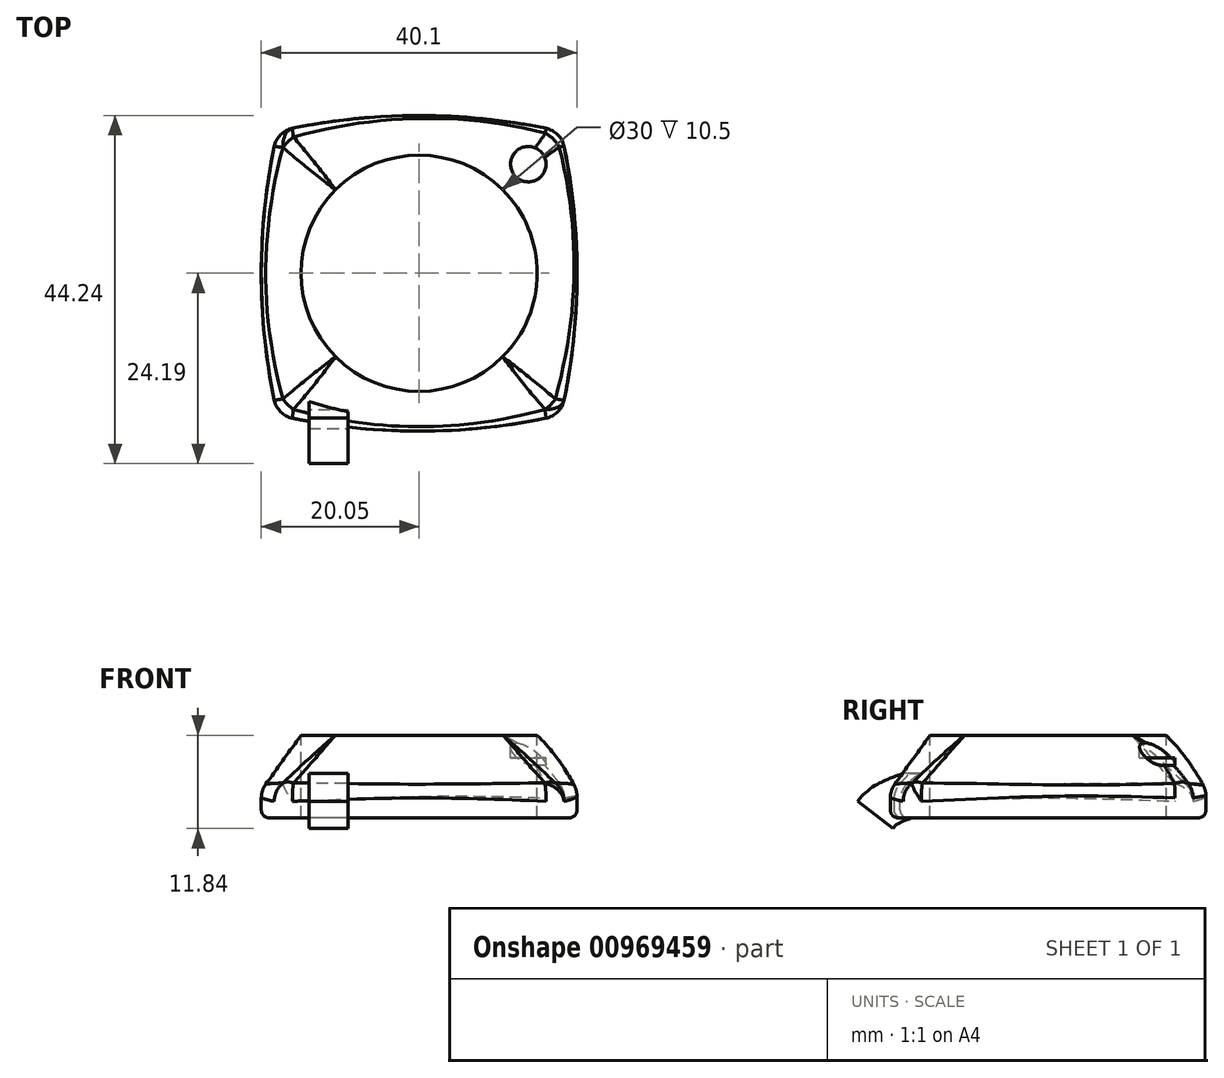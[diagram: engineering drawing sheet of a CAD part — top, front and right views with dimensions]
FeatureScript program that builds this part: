
annotation { "Feature Type Name" : "Feature", "Feature Type Description" : "" }
export const myFeature = defineFeature(function(context is Context, id is Id, definition is map)
    precondition{}
    {
        {
            assignVariable(context, id + "F0", {"name" : "base", "anyValue" : .333});
        }
        {
            assignVariable(context, id + "F1", {"name" : "Height", "anyValue" : 10.5});
        }
        {
            assignVariable(context, id + "F2", {"name" : "depth", "anyValue" : 2.9});
        }
        {
            var Q0;
            Q0=qCreatedBy(makeId("Top.planeOp"),FACE);
            var sketch = newSketch(context, id + "F3", { "sketchPlane" : qUnion([Q0])});
            skLineSegment(sketch, "E0.bottom", {"start": v(18, 18) * mm, "end": v(-18, 18) * mm});
            skLineSegment(sketch, "E0.top", {"start": v(18, -18) * mm, "end": v(-18, -18) * mm});
            skLineSegment(sketch, "E0.left", {"start": v(18, 18) * mm, "end": v(18, -18) * mm});
            skLineSegment(sketch, "E0.right", {"start": v(-18, 18) * mm, "end": v(-18, -18) * mm});
            skPoint(sketch, "E0.middle", {"position": v(0, 0) * mm});
            skArc(sketch, "E1", {"start": v(-18, 18) * mm, "mid": v(-20.05, 0) * mm, "end": v(-18, -18) * mm});
            skArc(sketch, "E2", {"start": v(18, 18) * mm, "mid": v(0, 20.05) * mm, "end": v(-18, 18) * mm});
            skArc(sketch, "E3.MirrorCS", {"start": v(18, -18) * mm, "mid": v(0, -20.05) * mm, "end": v(-18, -18) * mm});
            skArc(sketch, "E4.MirrorCS", {"start": v(18, 18) * mm, "mid": v(20.05, 0) * mm, "end": v(18, -18) * mm});
            skLineSegment(sketch, "E5", {"start": v(-18, 18) * mm, "end": v(18, -18) * mm, "construction": true});
            skLineSegment(sketch, "E6", {"start": v(18, 18) * mm, "end": v(-18, -18) * mm, "construction": true});
            skSolve(sketch);
        }
        {
            var Q0;
            Q0=qCreatedBy(makeId("Top.planeOp"),FACE);
            cPlane(context, id + "F4", {"entities" : qUnion([Q0]), "cplaneType" : CPlaneType.OFFSET, "offset" : ((1 - getVariable(context, 'base')) * getVariable(context, 'Height')) * mm, "width" : 150 * mm, "height" : 150 * mm});
        }
        {
            var Q0;
            Q0 = qSketchRegion(id + "F3", true);
            extrude(context, id + "F5", {"entities" : qUnion([Q0]), "oppositeDirection" : true, "depth" : (getVariable(context, 'base') * getVariable(context, 'Height')) * mm, "offsetDistance" : 25 * mm});
        }
        {
            var Q0;
            Q0=qCreatedBy(id+"F4.planeOp",FACE);
            var sketch = newSketch(context, id + "F6", { "sketchPlane" : qUnion([Q0])});
            skCircle(sketch, "E7", {"center": v(0, 0) * mm, "radius": 15 * mm});
            skPoint(sketch, "E8", {"position": v(15, 0) * mm});
            skPoint(sketch, "E9.1.0", {"position": v(10.6, 10.6) * mm});
            skPoint(sketch, "E9.2.0", {"position": v(0, 15) * mm});
            skPoint(sketch, "E9.3.0", {"position": v(-10.6, 10.6) * mm});
            skPoint(sketch, "E9.4.0", {"position": v(-15, 0) * mm});
            skPoint(sketch, "E9.5.0", {"position": v(-10.6, -10.6) * mm});
            skPoint(sketch, "E9.6.0", {"position": v(0, -15) * mm});
            skPoint(sketch, "E9.7.0", {"position": v(10.6, -10.6) * mm});
            skSolve(sketch);
        }
        {
            var Q0;
            Q0=makeQuery(id+"F5.opExtrude","SWEPT_EDGE",EDGE,{"disambiguationData":[OSD([sQuery(id+"F3.wireOp",EDGE,"E0.bottom"),sQuery(id+"F3.wireOp",EDGE,"E0.left"),sQuery(id+"F3.wireOp",EDGE,"E2"),sQuery(id+"F3.wireOp",EDGE,"E4.MirrorCS")])]});
            var Q1;
            Q1=sQuery(id+"F3.wireOp",VERTEX,"E0.middle");
            cPlane(context, id + "F7", {"entities" : qUnion([Q0, Q1]), "cplaneType" : CPlaneType.LINE_ANGLE, "offset" : 25 * mm, "angle" : 0 * degree, "oppositeDirection" : true, "width" : 150 * mm, "height" : 150 * mm});
        }
        {
            var Q0;
            Q0=qCreatedBy(id+"F7.planeOp",FACE);
            var sketch = newSketch(context, id + "F8", { "sketchPlane" : qUnion([Q0])});
            skArc(sketch, "E10", {"start": v(25.46, 0) * mm, "mid": v(20.68, 4.17) * mm, "end": v(15, 7) * mm});
            skLineSegment(sketch, "E11", {"start": v(0, 7.12) * mm, "end": v(0, 17.1) * mm});
            skSolve(sketch);
        }
        {
            var Q0;
            Q0=makeQuery(id+"F6.imprint","IMPRINT",FACE,{"disambiguationData":[TD([[makeQuery(id+"F6.imprint","IMPRINT",EDGE,{"derivedFrom":sQuery(id+"F6.wireOp",EDGE,"E7")}),1.0]])]});
            var Q1;
            Q1=makeQuery(id+"F5.opExtrude","CAP_FACE",FACE,{"disambiguationData":[OSD([sQuery(id+"F3.wireOp",EDGE,"E1"),sQuery(id+"F3.wireOp",EDGE,"E2"),sQuery(id+"F3.wireOp",EDGE,"E3.MirrorCS"),sQuery(id+"F3.wireOp",EDGE,"E4.MirrorCS")])],"isStart":true});
            var Q2;
            Q2=sQuery(id+"FI9qdWhZOXyrW1U_1.1.F8.wireOp",EDGE,"E10");
            var Q3;
            Q3=sQuery(id+"FI9qdWhZOXyrW1U_1.2.F8.wireOp",EDGE,"E10");
            var Q4;
            Q4=sQuery(id+"FI9qdWhZOXyrW1U_1.3.F8.wireOp",EDGE,"E10");
            var Q5;
            Q5=sQuery(id+"F8.wireOp",EDGE,"E10");
            loft(context, id + "F9", {"operationType" : NewBodyOperationType.ADD, "addGuides" : true, "sheetProfilesArray" : [{ "sheetProfileEntities" : qUnion([Q0]) }, { "sheetProfileEntities" : qUnion([Q1]) }], "guidesArray" : [{ "guideEntities" : qUnion([Q2]), "guideDerivativeType" : LoftGuideDerivativeType.DEFAULT, "guideDerivativeMagnitude" : 1 }, { "guideEntities" : qUnion([Q3]), "guideDerivativeType" : LoftGuideDerivativeType.DEFAULT, "guideDerivativeMagnitude" : 1 }, { "guideEntities" : qUnion([Q4]), "guideDerivativeType" : LoftGuideDerivativeType.DEFAULT, "guideDerivativeMagnitude" : 1 }, { "guideEntities" : qUnion([Q5]), "guideDerivativeType" : LoftGuideDerivativeType.DEFAULT, "guideDerivativeMagnitude" : 1 }]});
        }
        {
            var Q0;
            {var subQ0=sQuery(id+"F3.wireOp",EDGE,"E3.MirrorCS");Q0=makeQuery(id+"F9.boolean.opBoolean","MERGE",EDGE,{"derivedFrom":[makeQuery(id+"F5.opExtrude","CAP_EDGE",EDGE,{"disambiguationData":[OSD([subQ0])],"isStart":true}),makeQuery(id+"F9.opLoft","MID_CAP_EDGE",EDGE,{"disambiguationData":[OSD([sQuery(id+"F3.wireOp",EDGE,"E0.top"),sQuery(id+"F3.wireOp",EDGE,"E0.left"),sQuery(id+"F3.wireOp",EDGE,"E0.right"),sQuery(id+"F3.wireOp",EDGE,"E1"),subQ0,sQuery(id+"F3.wireOp",EDGE,"E4.MirrorCS")])],"capPos":1.0})]});}
            var Q1;
            {var subQ0=sQuery(id+"F3.wireOp",EDGE,"E4.MirrorCS");Q1=makeQuery(id+"F9.boolean.opBoolean","MERGE",EDGE,{"derivedFrom":[makeQuery(id+"F5.opExtrude","CAP_EDGE",EDGE,{"disambiguationData":[OSD([subQ0])],"isStart":true}),makeQuery(id+"F9.opLoft","MID_CAP_EDGE",EDGE,{"disambiguationData":[OSD([sQuery(id+"F3.wireOp",EDGE,"E0.bottom"),sQuery(id+"F3.wireOp",EDGE,"E0.top"),sQuery(id+"F3.wireOp",EDGE,"E0.left"),sQuery(id+"F3.wireOp",EDGE,"E2"),sQuery(id+"F3.wireOp",EDGE,"E3.MirrorCS"),subQ0])],"capPos":1.0})]});}
            var Q2;
            {var subQ0=sQuery(id+"F3.wireOp",EDGE,"E2");Q2=makeQuery(id+"F9.boolean.opBoolean","MERGE",EDGE,{"derivedFrom":[makeQuery(id+"F5.opExtrude","CAP_EDGE",EDGE,{"disambiguationData":[OSD([subQ0])],"isStart":true}),makeQuery(id+"F9.opLoft","MID_CAP_EDGE",EDGE,{"disambiguationData":[OSD([sQuery(id+"F3.wireOp",EDGE,"E0.bottom"),sQuery(id+"F3.wireOp",EDGE,"E0.left"),sQuery(id+"F3.wireOp",EDGE,"E0.right"),sQuery(id+"F3.wireOp",EDGE,"E1"),subQ0,sQuery(id+"F3.wireOp",EDGE,"E4.MirrorCS")])],"capPos":1.0})]});}
            var Q3;
            {var subQ0=sQuery(id+"F3.wireOp",EDGE,"E1");Q3=makeQuery(id+"F9.boolean.opBoolean","MERGE",EDGE,{"derivedFrom":[makeQuery(id+"F5.opExtrude","CAP_EDGE",EDGE,{"disambiguationData":[OSD([subQ0])],"isStart":true}),makeQuery(id+"F9.opLoft","MID_CAP_EDGE",EDGE,{"disambiguationData":[OSD([sQuery(id+"F3.wireOp",EDGE,"E0.bottom"),sQuery(id+"F3.wireOp",EDGE,"E0.top"),sQuery(id+"F3.wireOp",EDGE,"E0.right"),subQ0,sQuery(id+"F3.wireOp",EDGE,"E2"),sQuery(id+"F3.wireOp",EDGE,"E3.MirrorCS")])],"capPos":1.0})]});}
            fillet(context, id + "F10", {"entities" : qUnion([Q0, Q1, Q2, Q3]), "radius" : 3 * mm, "tangentPropagation" : true, "allowEdgeOverflow" : false});
        }
        {
            var Q0;
            Q0=makeQuery(id+"F6.imprint","IMPRINT",FACE,{"disambiguationData":[TD([[makeQuery(id+"F6.imprint","IMPRINT",EDGE,{"derivedFrom":sQuery(id+"F6.wireOp",EDGE,"E7")}),1.0]])]});
            var sketch = newSketch(context, id + "F11", { "sketchPlane" : qUnion([Q0])});
            skCircle(sketch, "E12", {"center": v(13.86, 13.86) * mm, "radius": 2.25 * mm});
            skLineSegment(sketch, "E13", {"start": v(10.6, 10.6) * mm, "end": v(13.86, 13.86) * mm, "construction": true});
            skPoint(sketch, "E14", {"position": v(10.6, 10.6) * mm});
            skSolve(sketch);
        }
        {
            var Q0;
            Q0=makeQuery(id+"F9.opLoft","SWEPT_EDGE",EDGE,{"disambiguationData":[OSD([sQuery(id+"F3.wireOp",EDGE,"E0.bottom"),sQuery(id+"F3.wireOp",EDGE,"E0.top"),sQuery(id+"F3.wireOp",EDGE,"E0.right"),sQuery(id+"F3.wireOp",EDGE,"E1"),sQuery(id+"F3.wireOp",EDGE,"E2"),sQuery(id+"F3.wireOp",EDGE,"E3.MirrorCS"),sQuery(id+"F6.wireOp",EDGE,"E7")])]});
            var Q1;
            Q1=makeQuery(id+"F9.opLoft","SWEPT_EDGE",EDGE,{"disambiguationData":[OSD([sQuery(id+"F8.wireOp",EDGE,"E10")])]});
            var Q2;
            Q2=makeQuery(id+"F9.opLoft","SWEPT_EDGE",EDGE,{"disambiguationData":[OSD([sQuery(id+"F3.wireOp",EDGE,"E0.top"),sQuery(id+"F3.wireOp",EDGE,"E0.left"),sQuery(id+"F3.wireOp",EDGE,"E3.MirrorCS"),sQuery(id+"F3.wireOp",EDGE,"E4.MirrorCS"),sQuery(id+"F6.wireOp",EDGE,"E7"),sQuery(id+"F8.wireOp",EDGE,"E10")])]});
            var Q3;
            Q3=makeQuery(id+"F9.opLoft","SWEPT_EDGE",EDGE,{"disambiguationData":[OSD([sQuery(id+"F3.wireOp",EDGE,"E0.top"),sQuery(id+"F3.wireOp",EDGE,"E0.left"),sQuery(id+"F3.wireOp",EDGE,"E0.right"),sQuery(id+"F3.wireOp",EDGE,"E1"),sQuery(id+"F3.wireOp",EDGE,"E3.MirrorCS"),sQuery(id+"F3.wireOp",EDGE,"E4.MirrorCS"),sQuery(id+"F6.wireOp",EDGE,"E7")])]});
            var Q4;
            Q4=makeQuery(id+"F9.opLoft","SWEPT_EDGE",EDGE,{"disambiguationData":[OSD([sQuery(id+"FI9qdWhZOXyrW1U_1.1.F8.wireOp",EDGE,"E10")])]});
            var Q5;
            Q5=makeQuery(id+"F9.opLoft","SWEPT_EDGE",EDGE,{"disambiguationData":[OSD([sQuery(id+"FI9qdWhZOXyrW1U_1.2.F8.wireOp",EDGE,"E10")])]});
            var Q6;
            Q6=makeQuery(id+"F9.opLoft","SWEPT_EDGE",EDGE,{"disambiguationData":[OSD([sQuery(id+"FI9qdWhZOXyrW1U_1.3.F8.wireOp",EDGE,"E10")])]});
            fillet(context, id + "F12", {"entities" : qUnion([Q0, Q1, Q2, Q3, Q4, Q5, Q6]), "radius" : 3 * mm, "tangentPropagation" : true, "allowEdgeOverflow" : false});
        }
        {
            var Q0;
            Q0=makeQuery(id+"F11.imprint","IMPRINT",FACE,{"disambiguationData":[TD([[makeQuery(id+"F11.imprint","IMPRINT",EDGE,{"derivedFrom":sQuery(id+"F11.wireOp",EDGE,"E12")}),1.0]])]});
            extrude(context, id + "F13", {"entities" : qUnion([Q0]), "operationType" : NewBodyOperationType.REMOVE, "oppositeDirection" : true, "depth" : (getVariable(context, 'depth')) * mm, "offsetDistance" : 25 * mm});
        }
        {
            var Q0;
            Q0=makeQuery(id+"F13.boolean.opBoolean","COPY",FACE,{"derivedFrom":makeQuery(id+"F13.opExtrude","CAP_FACE",FACE,{"disambiguationData":[OSD([sQuery(id+"F11.wireOp",EDGE,"E12")])],"isStart":false})});
            var sketch = newSketch(context, id + "F14", { "sketchPlane" : qUnion([Q0])});
            skCircle(sketch, "E15", {"center": v(13.86, 13.86) * mm, "radius": 2.25 * mm});
            skSolve(sketch);
        }
        {
            var Q0;
            Q0 = qSketchRegion(id + "F14", true);
            extrude(context, id + "F15", {"entities" : qUnion([Q0]), "operationType" : NewBodyOperationType.ADD, "oppositeDirection" : true, "depth" : 5 * mm, "offsetDistance" : 25 * mm});
        }
        {
            var Q0;
            Q0=makeQuery(id+"F11.imprint","IMPRINT",FACE,{"disambiguationData":[TD([[makeQuery(id+"F11.imprint","IMPRINT",EDGE,{"derivedFrom":makeQuery(id+"F6.imprint","IMPRINT",EDGE,{"derivedFrom":sQuery(id+"F6.wireOp",EDGE,"E7")})}),1.0]])]});
            extrude(context, id + "F16", {"entities" : qUnion([Q0]), "operationType" : NewBodyOperationType.REMOVE, "oppositeDirection" : true, "depth" : 25 * mm, "offsetDistance" : 25 * mm});
        }
        {
            var Q0;
            Q0=makeQuery(id+"F5.opExtrude","CAP_EDGE",EDGE,{"disambiguationData":[OSD([sQuery(id+"F3.wireOp",EDGE,"E2")])],"isStart":false});
            fillet(context, id + "F17", {"entities" : qUnion([Q0]), "radius" : 1 * mm, "tangentPropagation" : true, "allowEdgeOverflow" : false});
        }
        {
            var Q0;
            Q0=qCreatedBy(makeId("Front.planeOp"),FACE);
            cPlane(context, id + "F18", {"entities" : qUnion([Q0]), "cplaneType" : CPlaneType.OFFSET, "offset" : 15.5 * mm, "width" : 150 * mm, "height" : 150 * mm});
        }
        {
            var Q0;
            Q0=qCreatedBy(id+"F18.planeOp",FACE);
            var sketch = newSketch(context, id + "F19", { "sketchPlane" : qUnion([Q0])});
            skLineSegment(sketch, "E16.bottom", {"start": v(-14, -3.5) * mm, "end": v(-9, -3.5) * mm});
            skLineSegment(sketch, "E16.top", {"start": v(-14, 2.16) * mm, "end": v(-9, 2.16) * mm});
            skLineSegment(sketch, "E16.left", {"start": v(-14, -3.5) * mm, "end": v(-14, 2.16) * mm});
            skLineSegment(sketch, "E16.right", {"start": v(-9, -3.5) * mm, "end": v(-9, 2.16) * mm});
            skSolve(sketch);
        }
        {
            var Q0;
            Q0=qCreatedBy(id+"F18.planeOp",FACE);
            var Q1;
            Q1=sQuery(id+"F19.wireOp",EDGE,"E16.right");
            cPlane(context, id + "F20", {"entities" : qUnion([Q0, Q1]), "cplaneType" : CPlaneType.LINE_ANGLE, "offset" : 25 * mm, "angle" : 90 * degree, "width" : 150 * mm, "height" : 150 * mm});
        }
        {
            var Q0;
            Q0=qCreatedBy(id+"F20.planeOp",FACE);
            var sketch = newSketch(context, id + "F21", { "sketchPlane" : qUnion([Q0])});
            skPoint(sketch, "E17", {"position": v(15.5, -3.5) * mm});
            skLineSegment(sketch, "E18", {"start": v(15.5, -3.5) * mm, "end": v(17.34, -3.5) * mm});
            skFitSpline(sketch, "E19", {"points": [v(17.34, -3.5) * mm, v(19.18, -4.3) * mm, v(19.7, -4.84) * mm], "startDerivative": vector(3.45, -1.28) * mm, "endDerivative": vector(1.09, -1.41) * mm});
            skSolve(sketch);
        }
        {
            var Q0;
            Q0 = qSketchRegion(id + "F19", true);
            var Q1;
            Q1 = qConstructionFilter(qBodyType(qCreatedBy(id + "F21" ,EDGE), BodyType.WIRE), ConstructionObject.NO);
            sweep(context, id + "F22", {"operationType" : NewBodyOperationType.ADD, "profiles" : qUnion([Q0]), "path" : qUnion([Q1])});
        }
    });
